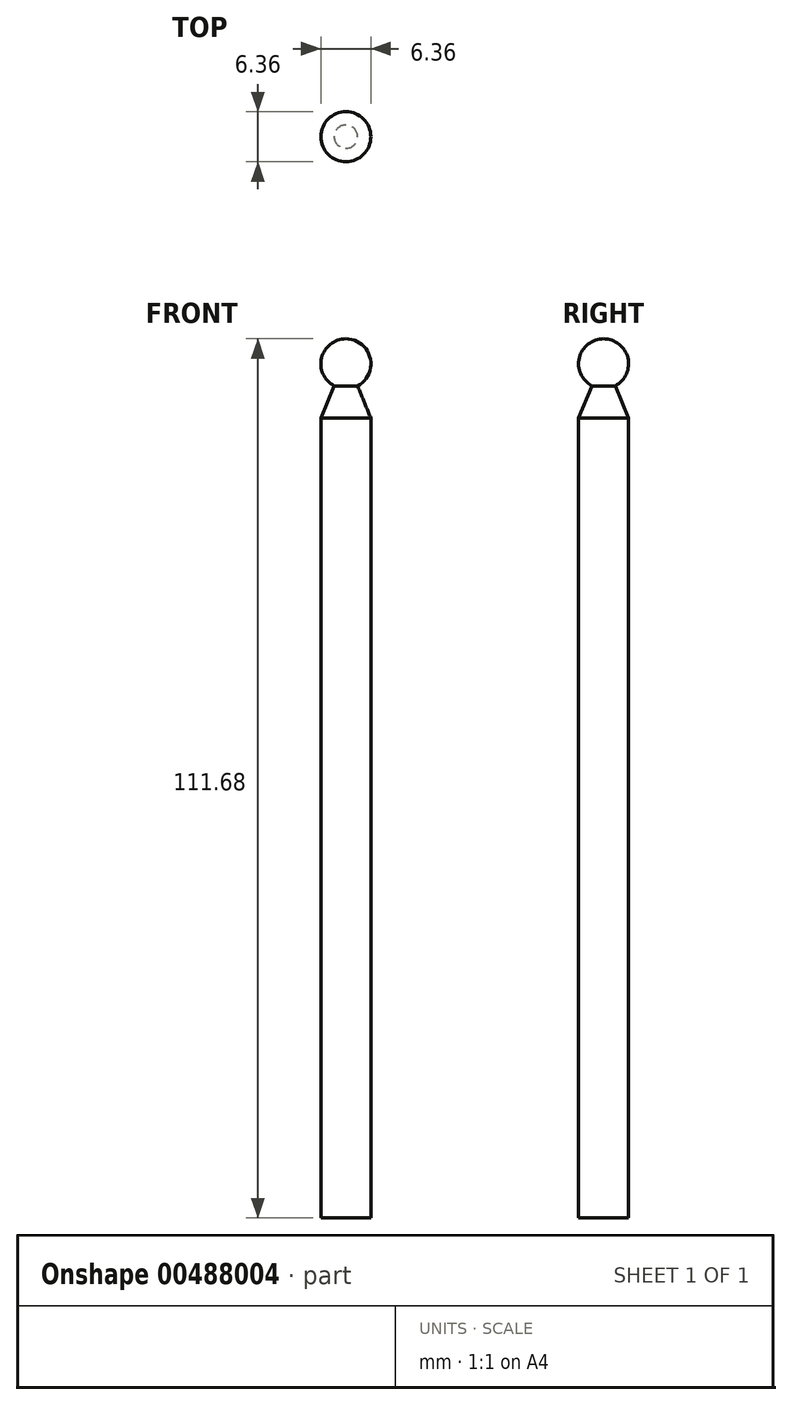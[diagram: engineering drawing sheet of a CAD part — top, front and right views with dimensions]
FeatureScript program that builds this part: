
annotation { "Feature Type Name" : "Feature", "Feature Type Description" : "" }
export const myFeature = defineFeature(function(context is Context, id is Id, definition is map)
    precondition{}
    {
        {
            var Q0;
            Q0=qCreatedBy(makeId("Top.planeOp"),FACE);
            var sketch = newSketch(context, id + "F0", { "sketchPlane" : qUnion([Q0])});
            skCircle(sketch, "E0", {"center": v(0, 0) * mm, "radius": 3.18 * mm});
            skSolve(sketch);
        }
        {
            var Q0;
            Q0=makeQuery(id+"F0.imprint","IMPRINT",FACE,{"disambiguationData":[TD([[makeQuery(id+"F0.imprint","IMPRINT",EDGE,{"derivedFrom":sQuery(id+"F0.wireOp",EDGE,"E0")}),1.0]])]});
            extrude(context, id + "F1", {"entities" : qUnion([Q0]), "depth" : 101.6 * mm});
        }
        {
            var Q0;
            Q0=qCreatedBy(makeId("Front.planeOp"),FACE);
            var sketch = newSketch(context, id + "F2", { "sketchPlane" : qUnion([Q0])});
            skLineSegment(sketch, "E1", {"start": v(0, 0) * mm, "end": v(0, 101.6) * mm});
            skLineSegment(sketch, "E2", {"start": v(0, 101.6) * mm, "end": v(-3.17, 101.6) * mm});
            skLineSegment(sketch, "E3", {"start": v(0, 101.6) * mm, "end": v(0, 108.5) * mm});
            skCircle(sketch, "E4", {"center": v(0, 108.5) * mm, "radius": 3.18 * mm});
            skLineSegment(sketch, "E5", {"start": v(-3.18, 101.6) * mm, "end": v(-1.49, 105.7) * mm});
            skLineSegment(sketch, "E6.MirrorCS", {"start": v(3.18, 101.6) * mm, "end": v(1.49, 105.7) * mm});
            skLineSegment(sketch, "E7", {"start": v(0, 108.5) * mm, "end": v(0, 111.68) * mm});
            skSolve(sketch);
        }
        {
            var Q0;
            {var subQ0=sQuery(id+"F2.wireOp",EDGE,"E7");Q0=makeQuery(id+"F2.imprint","IMPRINT",FACE,{"disambiguationData":[TD([[makeQuery(id+"F2.imprint","IMPRINT",EDGE,{"derivedFrom":subQ0}),1.0]])]});}
            var Q1;
            {var subQ0=sQuery(id+"F2.wireOp",EDGE,"E2");Q1=makeQuery(id+"F2.imprint","IMPRINT",FACE,{"disambiguationData":[TD([[makeQuery(id+"F2.imprint","IMPRINT",EDGE,{"derivedFrom":subQ0}),-1.0]])]});}
            var Q2;
            Q2=sQuery(id+"F2.wireOp",EDGE,"E3");
            revolve(context, id + "F3", {"operationType" : NewBodyOperationType.ADD, "entities" : qUnion([Q0, Q1]), "axis" : qUnion([Q2]), "revolveType" : RevolveType.FULL});
        }
    });
